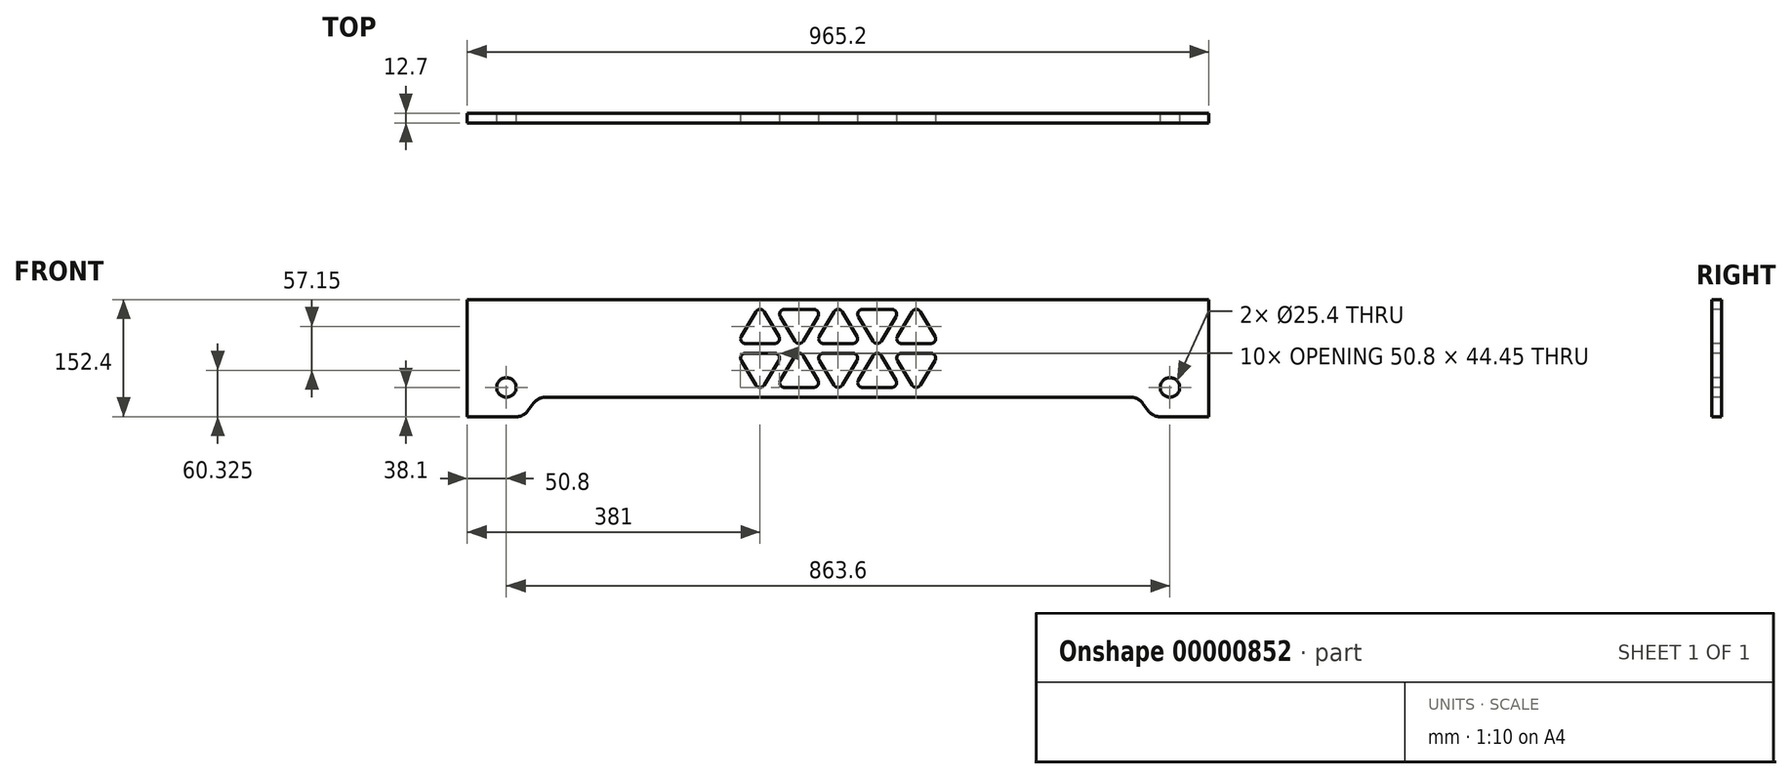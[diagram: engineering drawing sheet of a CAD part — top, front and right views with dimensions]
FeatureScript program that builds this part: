
annotation { "Feature Type Name" : "Feature", "Feature Type Description" : "" }
export const myFeature = defineFeature(function(context is Context, id is Id, definition is map)
    precondition{}
    {
        {
            var Q0;
            Q0=qCreatedBy(makeId("Front.planeOp"),FACE);
            var sketch = newSketch(context, id + "F0", { "sketchPlane" : qUnion([Q0])});
            skLineSegment(sketch, "E0.bottom", {"start": v(-482.6, 0) * mm, "end": v(0, 0) * mm});
            skLineSegment(sketch, "E0.top", {"start": v(-482.6, -152.4) * mm, "end": v(-419.1, -152.4) * mm});
            skLineSegment(sketch, "E0.left", {"start": v(-482.6, 0) * mm, "end": v(-482.6, -152.4) * mm});
            skLineSegment(sketch, "E1", {"start": v(-622.1, 0) * mm, "end": v(626.36, 0) * mm, "construction": true});
            skLineSegment(sketch, "E2", {"start": v(0, -127) * mm, "end": v(-381, -127) * mm});
            skLineSegment(sketch, "E3", {"start": v(-396.24, -134.62) * mm, "end": v(-403.86, -144.78) * mm});
            skPoint(sketch, "E4.visualSharp", {"position": v(-390.53, -127) * mm});
            skArc(sketch, "E4.filletArc", {"start": v(-381, -127) * mm, "mid": v(-389.52, -129.01) * mm, "end": v(-396.24, -134.62) * mm});
            skArc(sketch, "E5.filletArc", {"start": v(-419.1, -152.4) * mm, "mid": v(-410.58, -150.39) * mm, "end": v(-403.86, -144.78) * mm});
            skLineSegment(sketch, "E6", {"start": v(0, 0) * mm, "end": v(0, -12.7) * mm});
            skLineSegment(sketch, "E7", {"start": v(0, 0) * mm, "end": v(0, -12.7) * mm, "construction": true});
            skLineSegment(sketch, "E8", {"start": v(0, -69.85) * mm, "end": v(-19.05, -69.85) * mm});
            skLineSegment(sketch, "E9", {"start": v(-24.5, -79.47) * mm, "end": v(-5.45, -111.22) * mm});
            skLineSegment(sketch, "E10", {"start": v(0, -114.3) * mm, "end": v(0, -114.3) * mm});
            skLineSegment(sketch, "E11", {"start": v(0, -114.3) * mm, "end": v(0, -127) * mm});
            skPoint(sketch, "E12.visualSharp", {"position": v(-3.6, -114.3) * mm});
            skArc(sketch, "E12.filletArc", {"start": v(-5.45, -111.22) * mm, "mid": v(-3.13, -113.48) * mm, "end": v(0, -114.3) * mm});
            skLineSegment(sketch, "E13", {"start": v(0, -12.7) * mm, "end": v(0, -12.7) * mm});
            skLineSegment(sketch, "E14.trimOffspring", {"start": v(0, -57.15) * mm, "end": v(0, -69.85) * mm});
            skLineSegment(sketch, "E15.trimOffspring", {"start": v(0, -57.15) * mm, "end": v(0, -69.85) * mm, "construction": true});
            skLineSegment(sketch, "E16.trimOffspring", {"start": v(0, -114.3) * mm, "end": v(0, -127) * mm, "construction": true});
            skPoint(sketch, "E17.orphan", {"position": v(0, 143.15) * mm});
            skLineSegment(sketch, "E18", {"start": v(0, 51.96) * mm, "end": v(0, -165.59) * mm, "construction": true});
            skLineSegment(sketch, "E19", {"start": v(-584.93, -63.5) * mm, "end": v(217.94, -63.5) * mm, "construction": true});
            skLineSegment(sketch, "E20", {"start": v(-31.75, -114.3) * mm, "end": v(-69.85, -114.3) * mm});
            skLineSegment(sketch, "E21", {"start": v(-75.3, -104.68) * mm, "end": v(-56.25, -72.93) * mm});
            skLineSegment(sketch, "E22", {"start": v(-45.35, -72.93) * mm, "end": v(-26.3, -104.68) * mm});
            skLineSegment(sketch, "E23", {"start": v(-82.55, -69.85) * mm, "end": v(-120.65, -69.85) * mm});
            skLineSegment(sketch, "E24", {"start": v(-126.1, -79.47) * mm, "end": v(-107.05, -111.22) * mm});
            skLineSegment(sketch, "E25", {"start": v(-96.15, -111.22) * mm, "end": v(-77.1, -79.47) * mm});
            skPoint(sketch, "E26.visualSharp", {"position": v(-71.33, -69.85) * mm});
            skArc(sketch, "E26.filletArc", {"start": v(-77.1, -79.47) * mm, "mid": v(-77.02, -73.07) * mm, "end": v(-82.55, -69.85) * mm});
            skPoint(sketch, "E27.visualSharp", {"position": v(-131.87, -69.85) * mm});
            skArc(sketch, "E27.filletArc", {"start": v(-120.65, -69.85) * mm, "mid": v(-126.18, -73.07) * mm, "end": v(-126.1, -79.47) * mm});
            skPoint(sketch, "E28.visualSharp", {"position": v(-101.6, -120.3) * mm});
            skArc(sketch, "E28.filletArc", {"start": v(-107.05, -111.22) * mm, "mid": v(-101.6, -114.3) * mm, "end": v(-96.15, -111.22) * mm});
            skPoint(sketch, "E29.visualSharp", {"position": v(-81.07, -114.3) * mm});
            skArc(sketch, "E29.filletArc", {"start": v(-75.3, -104.68) * mm, "mid": v(-75.38, -111.08) * mm, "end": v(-69.85, -114.3) * mm});
            skPoint(sketch, "E30.visualSharp", {"position": v(-20.53, -114.3) * mm});
            skArc(sketch, "E30.filletArc", {"start": v(-31.75, -114.3) * mm, "mid": v(-26.22, -111.08) * mm, "end": v(-26.3, -104.68) * mm});
            skPoint(sketch, "E31.visualSharp", {"position": v(-50.8, -63.86) * mm});
            skArc(sketch, "E31.filletArc", {"start": v(-45.35, -72.93) * mm, "mid": v(-50.8, -69.85) * mm, "end": v(-56.25, -72.93) * mm});
            skPoint(sketch, "E32.visualSharp", {"position": v(-30.27, -69.85) * mm});
            skArc(sketch, "E32.filletArc", {"start": v(-19.05, -69.85) * mm, "mid": v(-24.58, -73.07) * mm, "end": v(-24.5, -79.47) * mm});
            skLineSegment(sketch, "E33.0.MirrorCS", {"start": v(0, -57.15) * mm, "end": v(-19.05, -57.15) * mm});
            skArc(sketch, "E34.0.MirrorCS", {"start": v(-19.05, -57.15) * mm, "mid": v(-24.58, -53.93) * mm, "end": v(-24.5, -47.53) * mm});
            skLineSegment(sketch, "E35.0.MirrorCS", {"start": v(-24.5, -47.53) * mm, "end": v(-5.45, -15.78) * mm});
            skArc(sketch, "E36.0.MirrorCS", {"start": v(-5.45, -15.78) * mm, "mid": v(-3.13, -13.52) * mm, "end": v(0, -12.7) * mm});
            skArc(sketch, "E37.0.MirrorCS", {"start": v(-31.75, -12.7) * mm, "mid": v(-26.22, -15.92) * mm, "end": v(-26.3, -22.32) * mm});
            skLineSegment(sketch, "E38.0.MirrorCS", {"start": v(-45.35, -54.07) * mm, "end": v(-26.3, -22.32) * mm});
            skLineSegment(sketch, "E39.0.MirrorCS", {"start": v(-31.75, -12.7) * mm, "end": v(-69.85, -12.7) * mm});
            skArc(sketch, "E40.0.MirrorCS", {"start": v(-75.3, -22.32) * mm, "mid": v(-75.38, -15.92) * mm, "end": v(-69.85, -12.7) * mm});
            skLineSegment(sketch, "E41.0.MirrorCS", {"start": v(-75.3, -22.32) * mm, "end": v(-56.25, -54.07) * mm});
            skArc(sketch, "E42.0.MirrorCS", {"start": v(-45.35, -54.07) * mm, "mid": v(-50.8, -57.15) * mm, "end": v(-56.25, -54.07) * mm});
            skArc(sketch, "E43.0.MirrorCS", {"start": v(-77.1, -47.53) * mm, "mid": v(-77.02, -53.93) * mm, "end": v(-82.55, -57.15) * mm});
            skLineSegment(sketch, "E44.0.MirrorCS", {"start": v(-82.55, -57.15) * mm, "end": v(-120.65, -57.15) * mm});
            skArc(sketch, "E45.0.MirrorCS", {"start": v(-120.65, -57.15) * mm, "mid": v(-126.18, -53.93) * mm, "end": v(-126.1, -47.53) * mm});
            skLineSegment(sketch, "E46.0.MirrorCS", {"start": v(-126.1, -47.53) * mm, "end": v(-107.05, -15.78) * mm});
            skArc(sketch, "E47.0.MirrorCS", {"start": v(-107.05, -15.78) * mm, "mid": v(-101.6, -12.7) * mm, "end": v(-96.15, -15.78) * mm});
            skLineSegment(sketch, "E48.0.MirrorCS", {"start": v(-96.15, -15.78) * mm, "end": v(-77.1, -47.53) * mm});
            skPoint(sketch, "E49", {"position": v(-431.8, -114.3) * mm});
            skPoint(sketch, "E50", {"position": v(-431.46, 14.43) * mm});
            skCircle(sketch, "E51", {"center": v(-431.8, -114.3) * mm, "radius": 12.7 * mm});
            skSolve(sketch);
        }
        {
            var Q0;
            Q0 = qSketchRegion(id + "F0", true);
            extrude(context, id + "F1", {"entities" : qUnion([Q0]), "oppositeDirection" : true, "depth" : 12.7 * mm});
        }
        {
            var Q0;
            Q0=makeQuery(id+"F1.opExtrude","SWEPT_BODY",BODY,{"disambiguationData":[OSD([sQuery(id+"F0.wireOp",EDGE,"E0.bottom"),sQuery(id+"F0.wireOp",EDGE,"E0.top"),sQuery(id+"F0.wireOp",EDGE,"E0.left"),sQuery(id+"F0.wireOp",EDGE,"E0.right")])]});
            var Q1;
            Q1=makeQuery(id+"F1.opExtrude","SWEPT_FACE",FACE,{"disambiguationData":[OSD([sQuery(id+"F0.wireOp",EDGE,"E6")])]});
            mirror(context, id + "F2", {"operationType" : NewBodyOperationType.ADD, "entities" : qUnion([Q0]), "mirrorPlane" : qUnion([Q1])});
        }
    });
